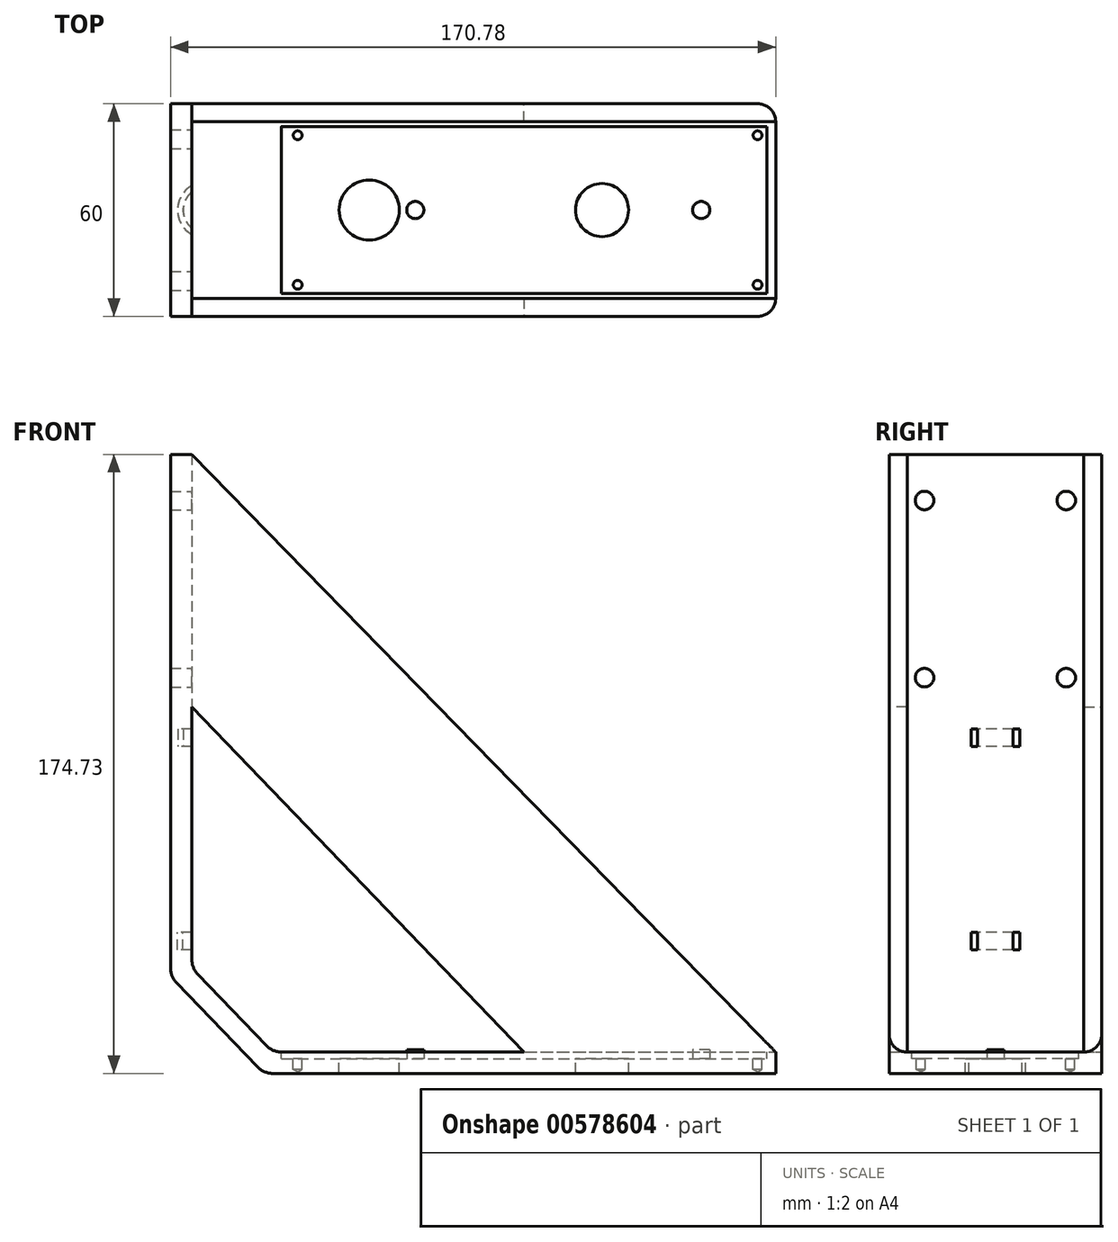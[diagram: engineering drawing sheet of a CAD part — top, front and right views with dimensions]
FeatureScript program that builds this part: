
annotation { "Feature Type Name" : "Feature", "Feature Type Description" : "" }
export const myFeature = defineFeature(function(context is Context, id is Id, definition is map)
    precondition{}
    {
        {
            var Q0;
            Q0=qCreatedBy(makeId("Front.planeOp"),FACE);
            var sketch = newSketch(context, id + "F0", { "sketchPlane" : qUnion([Q0])});
            skLineSegment(sketch, "E0", {"start": v(-28.83, 174.73) * mm, "end": v(-28.83, 29.73) * mm});
            skLineSegment(sketch, "E1", {"start": v(0, 0) * mm, "end": v(141.95, 0) * mm});
            skLineSegment(sketch, "E2", {"start": v(-28.83, 174.73) * mm, "end": v(-22.83, 174.73) * mm});
            skLineSegment(sketch, "E3", {"start": v(-22.83, 174.73) * mm, "end": v(-22.83, 29.73) * mm});
            skLineSegment(sketch, "E4", {"start": v(-22.83, 29.73) * mm, "end": v(0, 6) * mm});
            skLineSegment(sketch, "E5", {"start": v(0, 6) * mm, "end": v(141.95, 6) * mm});
            skLineSegment(sketch, "E6", {"start": v(141.95, 6) * mm, "end": v(141.95, 0) * mm});
            skLineSegment(sketch, "E7", {"start": v(0, 6) * mm, "end": v(0, 0) * mm, "construction": true});
            skLineSegment(sketch, "E8", {"start": v(-28.83, 29.73) * mm, "end": v(-22.83, 29.73) * mm, "construction": true});
            skLineSegment(sketch, "E9", {"start": v(-28.83, 29.73) * mm, "end": v(-28.83, 27.3) * mm});
            skLineSegment(sketch, "E10", {"start": v(-28.83, 27.3) * mm, "end": v(-2.55, 0) * mm});
            skLineSegment(sketch, "E11", {"start": v(-2.55, 0) * mm, "end": v(0, 0) * mm});
            skLineSegment(sketch, "E12", {"start": v(-22.83, 151.5) * mm, "end": v(-22.83, 174.73) * mm});
            skSolve(sketch);
        }
        {
            var Q0;
            Q0=makeQuery(id+"F0.imprint","IMPRINT",FACE,{"disambiguationData":[TD([[makeQuery(id+"F0.imprint","IMPRINT",EDGE,{"derivedFrom":sQuery(id+"F0.wireOp",EDGE,"E0")}),1.0]])]});
            extrude(context, id + "F1", {"entities" : qUnion([Q0]), "depth" : 60 * mm, "offsetDistance" : 25 * mm});
        }
        {
            var Q0;
            Q0=makeQuery(id+"F1.opExtrude","SWEPT_FACE",FACE,{"disambiguationData":[OSD([sQuery(id+"F0.wireOp",EDGE,"E5")])]});
            var sketch = newSketch(context, id + "F2", { "sketchPlane" : qUnion([Q0])});
            skLineSegment(sketch, "E13.bottom", {"start": v(2.47, -6.43) * mm, "end": v(139.47, -6.42) * mm});
            skLineSegment(sketch, "E13.top", {"start": v(2.47, -53.58) * mm, "end": v(139.47, -53.57) * mm});
            skLineSegment(sketch, "E13.left", {"start": v(2.47, -6.43) * mm, "end": v(2.47, -53.58) * mm});
            skLineSegment(sketch, "E13.right", {"start": v(139.47, -6.42) * mm, "end": v(139.47, -53.57) * mm});
            skSolve(sketch);
        }
        {
            var Q0;
            Q0=makeQuery(id+"F2.imprint","IMPRINT",FACE,{"disambiguationData":[TD([[makeQuery(id+"F2.imprint","IMPRINT",EDGE,{"derivedFrom":sQuery(id+"F2.wireOp",EDGE,"E13.bottom")}),-1.0]])]});
            extrude(context, id + "F3", {"entities" : qUnion([Q0]), "operationType" : NewBodyOperationType.REMOVE, "oppositeDirection" : true, "depth" : 1.85 * mm, "offsetDistance" : 25 * mm});
        }
        {
            var Q0;
            Q0=makeQuery(id+"F3.boolean.opBoolean","COPY",FACE,{"derivedFrom":makeQuery(id+"F3.opExtrude","CAP_FACE",FACE,{"disambiguationData":[OSD([sQuery(id+"F2.wireOp",EDGE,"E13.bottom"),sQuery(id+"F2.wireOp",EDGE,"E13.top"),sQuery(id+"F2.wireOp",EDGE,"E13.left"),sQuery(id+"F2.wireOp",EDGE,"E13.right")])],"isStart":false})});
            var sketch = newSketch(context, id + "F4", { "sketchPlane" : qUnion([Q0])});
            skPoint(sketch, "E14", {"position": v(136.82, -8.9) * mm});
            skPoint(sketch, "E15", {"position": v(136.82, -51.1) * mm});
            skPoint(sketch, "E16", {"position": v(7.02, -51.1) * mm});
            skPoint(sketch, "E17", {"position": v(7.02, -8.9) * mm});
            skPoint(sketch, "E18", {"position": v(40.22, -30) * mm});
            skPoint(sketch, "E19", {"position": v(120.92, -30) * mm});
            skCircle(sketch, "E20", {"center": v(40.22, -30) * mm, "radius": 2.43 * mm});
            skCircle(sketch, "E21", {"center": v(120.92, -30) * mm, "radius": 2.43 * mm});
            skLineSegment(sketch, "E22.bottom", {"start": v(2.72, -6.5) * mm, "end": v(139.22, -6.5) * mm});
            skLineSegment(sketch, "E22.top", {"start": v(2.72, -53.5) * mm, "end": v(139.22, -53.5) * mm});
            skLineSegment(sketch, "E22.left", {"start": v(2.72, -6.5) * mm, "end": v(2.72, -53.5) * mm});
            skLineSegment(sketch, "E22.right", {"start": v(139.22, -6.5) * mm, "end": v(139.22, -53.5) * mm});
            skLineSegment(sketch, "E23", {"start": v(120.92, -30) * mm, "end": v(92.92, -30) * mm, "construction": true});
            skLineSegment(sketch, "E24", {"start": v(40.22, -30) * mm, "end": v(27.22, -30) * mm, "construction": true});
            skCircle(sketch, "E25", {"center": v(27.22, -30) * mm, "radius": 8.5 * mm});
            skCircle(sketch, "E26", {"center": v(92.92, -30) * mm, "radius": 7.5 * mm});
            skSolve(sketch);
        }
        {
            var Q0;
            Q0=sQuery(id+"F4.wireOp",VERTEX,"E17");
            var Q1;
            Q1=sQuery(id+"F4.wireOp",VERTEX,"E14");
            var Q2;
            Q2=sQuery(id+"F4.wireOp",VERTEX,"E15");
            var Q3;
            Q3=sQuery(id+"F4.wireOp",VERTEX,"E16");
            var Q4;
            Q4=makeQuery(id+"F1.opExtrude","SWEPT_BODY",BODY,{"disambiguationData":[OSD([sQuery(id+"F0.wireOp",EDGE,"E0"),sQuery(id+"F0.wireOp",EDGE,"pjV70WAZ-Rcya-7Rw0-g60Y-Jp7lQ99mjT5H"),sQuery(id+"F0.wireOp",EDGE,"E1"),sQuery(id+"F0.wireOp",EDGE,"E2"),sQuery(id+"F0.wireOp",EDGE,"E3"),sQuery(id+"F0.wireOp",EDGE,"E4"),sQuery(id+"F0.wireOp",EDGE,"E5"),sQuery(id+"F0.wireOp",EDGE,"E6")])]});
            hole(context, id + "F5", {"style" : HoleStyle.SIMPLE, "endStyle" : HoleEndStyle.BLIND, "holeDiameter" : 2.5 * mm, "holeDepth" : 3 * mm, "isTappedThrough" : true, "tappedDepth" : 12 * mm, "tapClearance" : 3, "locations" : qUnion([Q0, Q1, Q2, Q3]), "scope" : qUnion([Q4]), "majorDiameter" : 5 * mm});
        }
        {
            var Q0;
            Q0=makeQuery(id+"F4.imprint","IMPRINT",FACE,{"disambiguationData":[TD([[makeQuery(id+"F4.imprint","IMPRINT",EDGE,{"derivedFrom":sQuery(id+"F4.wireOp",EDGE,"E20")}),1.0]])]});
            var Q1;
            Q1=makeQuery(id+"F4.imprint","IMPRINT",FACE,{"disambiguationData":[TD([[makeQuery(id+"F4.imprint","IMPRINT",EDGE,{"derivedFrom":sQuery(id+"F4.wireOp",EDGE,"E21")}),1.0]])]});
            extrude(context, id + "F6", {"entities" : qUnion([Q0, Q1]), "operationType" : NewBodyOperationType.ADD, "depth" : 2.5 * mm, "offsetDistance" : 25 * mm});
        }
        {
            var Q0;
            Q0=makeQuery(id+"F1.opExtrude","SWEPT_FACE",FACE,{"disambiguationData":[OSD([sQuery(id+"F0.wireOp",EDGE,"E3")])]});
            var sketch = newSketch(context, id + "F7", { "sketchPlane" : qUnion([Q0])});
            skLineSegment(sketch, "E27.bottom", {"start": v(-50, 174.73) * mm, "end": v(-10, 174.73) * mm, "construction": true});
            skLineSegment(sketch, "E27.top", {"start": v(-50, 96.73) * mm, "end": v(-10, 96.73) * mm, "construction": true});
            skLineSegment(sketch, "E27.left", {"start": v(-50, 174.73) * mm, "end": v(-50, 96.73) * mm, "construction": true});
            skLineSegment(sketch, "E27.right", {"start": v(-10, 174.73) * mm, "end": v(-10, 96.73) * mm, "construction": true});
            skPoint(sketch, "E28", {"position": v(-50, 161.73) * mm});
            skPoint(sketch, "E29", {"position": v(-10, 161.73) * mm});
            skPoint(sketch, "E30", {"position": v(-50, 111.73) * mm});
            skPoint(sketch, "E31", {"position": v(-10, 111.73) * mm});
            skLineSegment(sketch, "E32", {"start": v(-30, 174.73) * mm, "end": v(-30, 29.73) * mm, "construction": true});
            skLineSegment(sketch, "E33", {"start": v(-60, 99.73) * mm, "end": v(0, 99.73) * mm, "construction": true});
            skLineSegment(sketch, "E34", {"start": v(-60, 94.73) * mm, "end": v(0, 94.73) * mm, "construction": true});
            skSolve(sketch);
        }
        {
            var Q0;
            Q0=sQuery(id+"F7.wireOp",VERTEX,"E28");
            var Q1;
            Q1=sQuery(id+"F7.wireOp",VERTEX,"E29");
            var Q2;
            Q2=sQuery(id+"F7.wireOp",VERTEX,"E31");
            var Q3;
            Q3=sQuery(id+"F7.wireOp",VERTEX,"E30");
            var Q4;
            Q4=sQuery(id+"F7.wireOp",VERTEX,"d87060a9-d560-4328-90d6-120cbc4be284");
            var Q5;
            Q5=sQuery(id+"F7.wireOp",VERTEX,"b24fa170-ac1a-4f8a-a9ad-690cf26e2aba");
            var Q6;
            Q6=makeQuery(id+"F1.opExtrude","SWEPT_BODY",BODY,{"disambiguationData":[OSD([sQuery(id+"F0.wireOp",EDGE,"E0"),sQuery(id+"F0.wireOp",EDGE,"pjV70WAZ-Rcya-7Rw0-g60Y-Jp7lQ99mjT5H"),sQuery(id+"F0.wireOp",EDGE,"E1"),sQuery(id+"F0.wireOp",EDGE,"E2"),sQuery(id+"F0.wireOp",EDGE,"E3"),sQuery(id+"F0.wireOp",EDGE,"E4"),sQuery(id+"F0.wireOp",EDGE,"E5"),sQuery(id+"F0.wireOp",EDGE,"E6")])]});
            hole(context, id + "F8", {"style" : HoleStyle.SIMPLE, "endStyle" : HoleEndStyle.THROUGH, "holeDiameter" : 5.25 * mm, "isTappedThrough" : true, "tappedDepth" : 12 * mm, "tapClearance" : 3, "locations" : qUnion([Q0, Q1, Q2, Q3, Q4, Q5]), "scope" : qUnion([Q6]), "majorDiameter" : 5 * mm});
        }
        {
            var Q0;
            Q0=makeQuery(id+"F1.opExtrude","SWEPT_EDGE",EDGE,{"disambiguationData":[OSD([sQuery(id+"F0.wireOp",EDGE,"E3"),sQuery(id+"F0.wireOp",EDGE,"E4")])]});
            var Q1;
            Q1=makeQuery(id+"F1.opExtrude","SWEPT_EDGE",EDGE,{"disambiguationData":[OSD([sQuery(id+"F0.wireOp",EDGE,"E4"),sQuery(id+"F0.wireOp",EDGE,"E5")])]});
            var Q2;
            Q2=makeQuery(id+"F1.opExtrude","SWEPT_EDGE",EDGE,{"disambiguationData":[OSD([sQuery(id+"F0.wireOp",EDGE,"E9"),sQuery(id+"F0.wireOp",EDGE,"E10")])]});
            var Q3;
            Q3=makeQuery(id+"F1.opExtrude","SWEPT_EDGE",EDGE,{"disambiguationData":[OSD([sQuery(id+"F0.wireOp",EDGE,"E10"),sQuery(id+"F0.wireOp",EDGE,"E11")])]});
            fillet(context, id + "F9", {"entities" : qUnion([Q0, Q1, Q2, Q3]), "radius" : 6 * mm, "tangentPropagation" : true, "allowEdgeOverflow" : false});
        }
        {
            var Q0;
            Q0=makeQuery(id+"F4.imprint","IMPRINT",FACE,{"disambiguationData":[TD([[makeQuery(id+"F4.imprint","IMPRINT",EDGE,{"derivedFrom":sQuery(id+"F4.wireOp",EDGE,"E25")}),1.0]])]});
            var Q1;
            Q1=makeQuery(id+"F4.imprint","IMPRINT",FACE,{"disambiguationData":[TD([[makeQuery(id+"F4.imprint","IMPRINT",EDGE,{"derivedFrom":sQuery(id+"F4.wireOp",EDGE,"E26")}),1.0]])]});
            extrude(context, id + "F10", {"entities" : qUnion([Q0, Q1]), "operationType" : NewBodyOperationType.REMOVE, "oppositeDirection" : true, "depth" : 25 * mm, "offsetDistance" : 25 * mm});
        }
        {
            var Q0;
            Q0=makeQuery(id+"F1.opExtrude","CAP_FACE",FACE,{"disambiguationData":[OSD([sQuery(id+"F0.wireOp",EDGE,"E0"),sQuery(id+"F0.wireOp",EDGE,"E1"),sQuery(id+"F0.wireOp",EDGE,"E2"),sQuery(id+"F0.wireOp",EDGE,"E3"),sQuery(id+"F0.wireOp",EDGE,"E4"),sQuery(id+"F0.wireOp",EDGE,"E5"),sQuery(id+"F0.wireOp",EDGE,"E6"),sQuery(id+"F0.wireOp",EDGE,"E9"),sQuery(id+"F0.wireOp",EDGE,"E10"),sQuery(id+"F0.wireOp",EDGE,"E11"),sQuery(id+"F0.wireOp",EDGE,"E12")])],"isStart":true});
            var sketch = newSketch(context, id + "F11", { "sketchPlane" : qUnion([Q0])});
            skLineSegment(sketch, "E35", {"start": v(22.83, 174.73) * mm, "end": v(-141.95, 6) * mm});
            skLineSegment(sketch, "E36", {"start": v(-141.95, 6) * mm, "end": v(-70.94, 6) * mm});
            skLineSegment(sketch, "E37", {"start": v(-70.94, 6) * mm, "end": v(22.83, 103.44) * mm});
            skLineSegment(sketch, "E38", {"start": v(22.83, 103.44) * mm, "end": v(22.83, 174.73) * mm});
            skPoint(sketch, "E39", {"position": v(22.83, 103.44) * mm});
            skSolve(sketch);
        }
        {
            var Q0;
            Q0=makeQuery(id+"F11.imprint","IMPRINT",FACE,{"disambiguationData":[TD([[makeQuery(id+"F11.imprint","IMPRINT",EDGE,{"derivedFrom":sQuery(id+"F11.wireOp",EDGE,"E35")}),1.0]])]});
            extrude(context, id + "F12", {"entities" : qUnion([Q0]), "operationType" : NewBodyOperationType.ADD, "oppositeDirection" : true, "depth" : 5.1 * mm, "offsetDistance" : 25 * mm});
        }
        {
            var Q0;
            Q0=makeQuery(id+"F1.opExtrude","CAP_FACE",FACE,{"disambiguationData":[OSD([sQuery(id+"F0.wireOp",EDGE,"E0"),sQuery(id+"F0.wireOp",EDGE,"E1"),sQuery(id+"F0.wireOp",EDGE,"E2"),sQuery(id+"F0.wireOp",EDGE,"E3"),sQuery(id+"F0.wireOp",EDGE,"E4"),sQuery(id+"F0.wireOp",EDGE,"E5"),sQuery(id+"F0.wireOp",EDGE,"E6"),sQuery(id+"F0.wireOp",EDGE,"E9"),sQuery(id+"F0.wireOp",EDGE,"E10"),sQuery(id+"F0.wireOp",EDGE,"E11"),sQuery(id+"F0.wireOp",EDGE,"E12")])],"isStart":false});
            var sketch = newSketch(context, id + "F13", { "sketchPlane" : qUnion([Q0])});
            skLineSegment(sketch, "E40", {"start": v(-22.83, 174.73) * mm, "end": v(141.95, 6) * mm});
            skLineSegment(sketch, "E41", {"start": v(-22.83, 103.44) * mm, "end": v(70.94, 6) * mm});
            skPoint(sketch, "E42", {"position": v(-22.83, 103.44) * mm});
            skSolve(sketch);
        }
        {
            var Q0;
            {var subQ0=sQuery(id+"F13.wireOp",EDGE,"E40");Q0=makeQuery(id+"F13.imprint","IMPRINT",FACE,{"disambiguationData":[TD([[makeQuery(id+"F13.imprint","IMPRINT",EDGE,{"derivedFrom":subQ0}),-1.0]])]});}
            extrude(context, id + "F14", {"entities" : qUnion([Q0]), "operationType" : NewBodyOperationType.ADD, "oppositeDirection" : true, "depth" : 5.1 * mm, "offsetDistance" : 25 * mm});
        }
        {
            var Q0;
            Q0=makeQuery(id+"F1.opExtrude","CAP_EDGE",EDGE,{"disambiguationData":[OSD([sQuery(id+"F0.wireOp",EDGE,"E6")])],"isStart":false});
            var Q1;
            Q1=makeQuery(id+"F1.opExtrude","CAP_EDGE",EDGE,{"disambiguationData":[OSD([sQuery(id+"F0.wireOp",EDGE,"E6")])],"isStart":true});
            fillet(context, id + "F15", {"entities" : qUnion([Q0, Q1]), "radius" : 5 * mm, "tangentPropagation" : true, "allowEdgeOverflow" : false});
        }
        {
            var Q0;
            Q0=sQuery(id+"F7.wireOp",EDGE,"E34");
            cPlane(context, id + "F16", {"entities" : qUnion([Q0]), "cplaneType" : CPlaneType.LINE_ANGLE, "offset" : 25 * mm, "angle" : 0 * degree, "width" : 150 * mm, "height" : 150 * mm});
        }
        {
            var Q0;
            Q0=qCreatedBy(id+"F16.planeOp",FACE);
            var sketch = newSketch(context, id + "F17", { "sketchPlane" : qUnion([Q0])});
            skArc(sketch, "E43", {"start": v(-22.83, -23.12) * mm, "mid": v(-26.83, -30) * mm, "end": v(-22.83, -36.88) * mm});
            skArc(sketch, "E44", {"start": v(-22.83, -25) * mm, "mid": v(-25.27, -30) * mm, "end": v(-22.83, -35) * mm});
            skLineSegment(sketch, "E45", {"start": v(-22.83, -23.12) * mm, "end": v(-21.59, -23.12) * mm});
            skLineSegment(sketch, "E46", {"start": v(-22.83, -25) * mm, "end": v(-21.59, -25) * mm});
            skLineSegment(sketch, "E47", {"start": v(-21.59, -25) * mm, "end": v(-21.59, -23.12) * mm});
            skLineSegment(sketch, "E48", {"start": v(-22.83, -35) * mm, "end": v(-21.7, -35) * mm});
            skLineSegment(sketch, "E49", {"start": v(-22.83, -36.88) * mm, "end": v(-21.7, -36.88) * mm});
            skLineSegment(sketch, "E50", {"start": v(-21.7, -36.88) * mm, "end": v(-21.7, -35) * mm});
            skSolve(sketch);
        }
        {
            var Q0;
            Q0=makeQuery(id+"F17.imprint","IMPRINT",FACE,{"disambiguationData":[TD([[makeQuery(id+"F17.imprint","IMPRINT",EDGE,{"derivedFrom":sQuery(id+"F17.wireOp",EDGE,"E43")}),1.0]])]});
            extrude(context, id + "F18", {"entities" : qUnion([Q0]), "operationType" : NewBodyOperationType.REMOVE, "endBound" : BoundingType.SYMMETRIC, "depth" : 5 * mm, "offsetDistance" : 25 * mm});
        }
        {
            var Q0;
            Q0=qCreatedBy(id+"F16.planeOp",FACE);
            cPlane(context, id + "F19", {"entities" : qUnion([Q0]), "cplaneType" : CPlaneType.OFFSET, "offset" : 57.4 * mm, "oppositeDirection" : true, "width" : 150 * mm, "height" : 150 * mm});
        }
        {
            var Q0;
            Q0=qCreatedBy(id+"F19.planeOp",FACE);
            var sketch = newSketch(context, id + "F20", { "sketchPlane" : qUnion([Q0])});
            skArc(sketch, "E51", {"start": v(-22.9, -23.12) * mm, "mid": v(-26.9, -30) * mm, "end": v(-22.9, -36.88) * mm});
            skArc(sketch, "E52", {"start": v(-22.9, -25) * mm, "mid": v(-25.34, -30) * mm, "end": v(-22.9, -35) * mm});
            skLineSegment(sketch, "E53", {"start": v(-22.9, -23.12) * mm, "end": v(-21.66, -23.12) * mm});
            skLineSegment(sketch, "E54", {"start": v(-22.9, -25) * mm, "end": v(-21.66, -25) * mm});
            skLineSegment(sketch, "E55", {"start": v(-21.66, -25) * mm, "end": v(-21.66, -23.12) * mm});
            skLineSegment(sketch, "E56", {"start": v(-22.9, -35) * mm, "end": v(-21.77, -35) * mm});
            skLineSegment(sketch, "E57", {"start": v(-22.9, -36.88) * mm, "end": v(-21.77, -36.88) * mm});
            skLineSegment(sketch, "E58", {"start": v(-21.77, -36.88) * mm, "end": v(-21.77, -35) * mm});
            skSolve(sketch);
        }
        {
            var Q0;
            Q0=makeQuery(id+"F20.imprint","IMPRINT",FACE,{"disambiguationData":[TD([[makeQuery(id+"F20.imprint","IMPRINT",EDGE,{"derivedFrom":sQuery(id+"F20.wireOp",EDGE,"E51")}),1.0]])]});
            var Q1;
            Q1=sQuery(id+"F20.wireOp",EDGE,"E51");
            var Q2;
            Q2=sQuery(id+"F20.wireOp",EDGE,"E52");
            var Q3;
            Q3=sQuery(id+"F20.wireOp",EDGE,"E53");
            var Q4;
            Q4=sQuery(id+"F20.wireOp",EDGE,"E54");
            var Q5;
            Q5=sQuery(id+"F20.wireOp",EDGE,"E55");
            var Q6;
            Q6=sQuery(id+"F20.wireOp",EDGE,"E56");
            var Q7;
            Q7=sQuery(id+"F20.wireOp",EDGE,"E57");
            var Q8;
            Q8=sQuery(id+"F20.wireOp",EDGE,"E58");
            extrude(context, id + "F21", {"entities" : qUnion([Q0]), "operationType" : NewBodyOperationType.REMOVE, "surfaceEntities" : qUnion([Q1, Q2, Q3, Q4, Q5, Q6, Q7, Q8]), "endBound" : BoundingType.SYMMETRIC, "oppositeDirection" : true, "depth" : 5 * mm, "offsetDistance" : 25 * mm});
        }
    });
